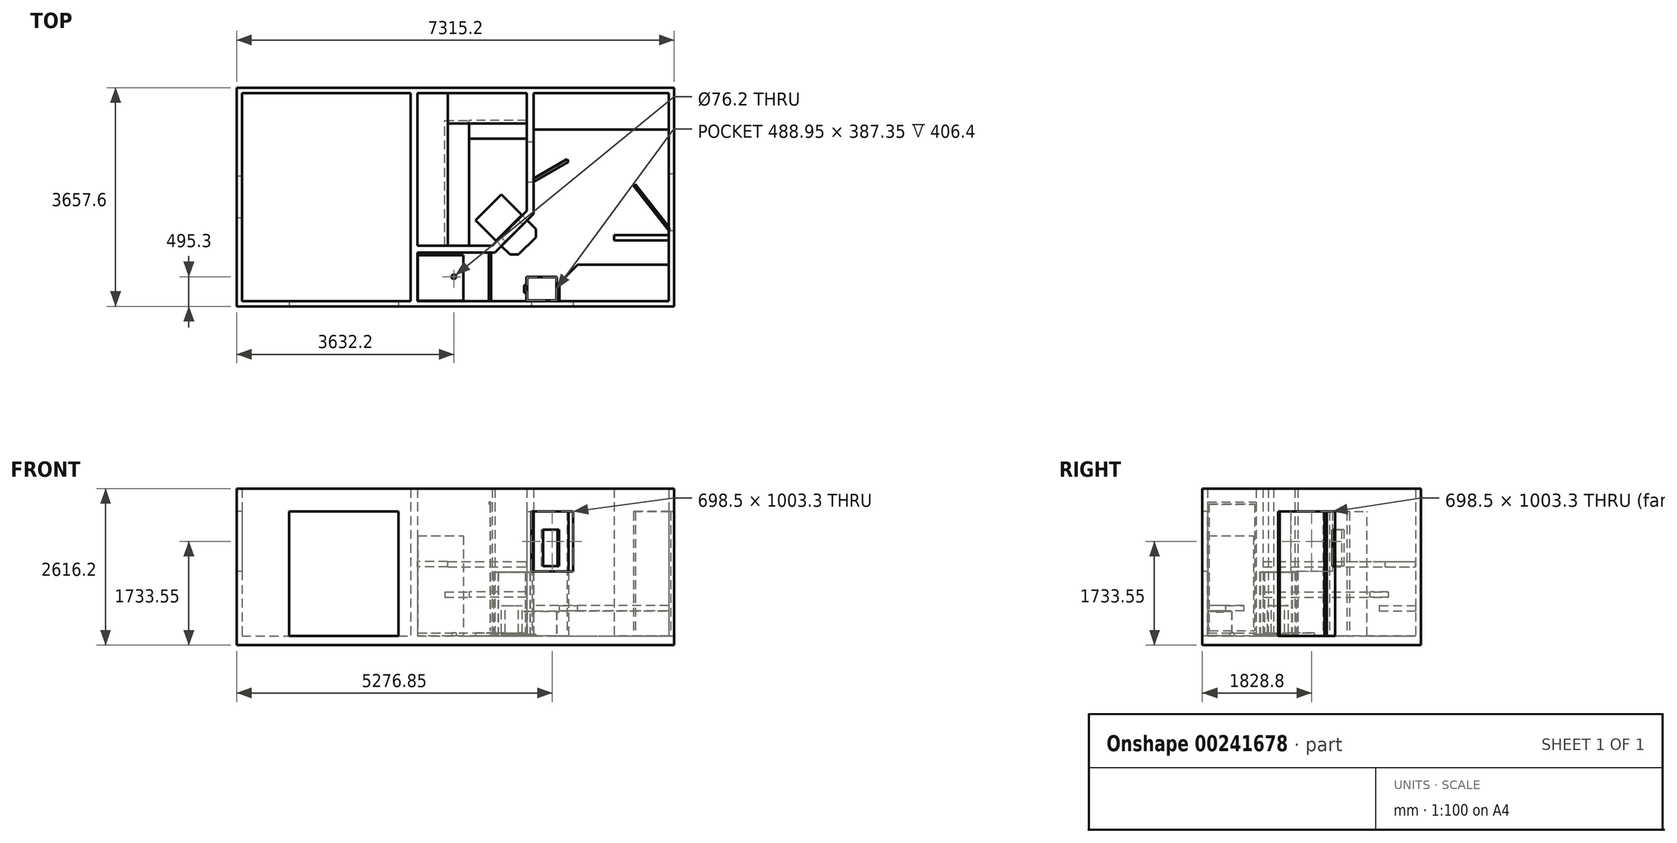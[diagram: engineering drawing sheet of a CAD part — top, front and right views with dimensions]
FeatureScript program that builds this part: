
annotation { "Feature Type Name" : "Feature", "Feature Type Description" : "" }
export const myFeature = defineFeature(function(context is Context, id is Id, definition is map)
    precondition{}
    {
        {
            var Q0;
            Q0=qCreatedBy(makeId("Top.planeOp"),FACE);
            var sketch = newSketch(context, id + "F0", { "sketchPlane" : qUnion([Q0])});
            skLineSegment(sketch, "E0.bottom", {"start": v(-3657.6, -1828.8) * mm, "end": v(3657.6, -1828.8) * mm});
            skLineSegment(sketch, "E0.top", {"start": v(-3657.6, 1828.8) * mm, "end": v(3657.6, 1828.8) * mm});
            skLineSegment(sketch, "E0.left", {"start": v(-3657.6, -1828.8) * mm, "end": v(-3657.6, 1828.8) * mm});
            skLineSegment(sketch, "E0.right", {"start": v(3657.6, -1828.8) * mm, "end": v(3657.6, 1828.8) * mm});
            skPoint(sketch, "E0.middle", {"position": v(0, 0) * mm});
            skSolve(sketch);
        }
        {
            var Q0;
            Q0=makeQuery(id+"F0.imprint","IMPRINT",FACE,{"disambiguationData":[TD([[makeQuery(id+"F0.imprint","IMPRINT",EDGE,{"derivedFrom":sQuery(id+"F0.wireOp",EDGE,"E0.bottom")}),1.0]])]});
            extrude(context, id + "F1", {"entities" : qUnion([Q0]), "depth" : 152.4 * mm});
        }
        {
            var Q0;
            Q0=makeQuery(id+"F1.opExtrude","CAP_FACE",FACE,{"disambiguationData":[OSD([sQuery(id+"F0.wireOp",EDGE,"E0.bottom"),sQuery(id+"F0.wireOp",EDGE,"E0.top"),sQuery(id+"F0.wireOp",EDGE,"E0.left"),sQuery(id+"F0.wireOp",EDGE,"E0.right")])],"isStart":false});
            var sketch = newSketch(context, id + "F2", { "sketchPlane" : qUnion([Q0])});
            skLineSegment(sketch, "E1.0", {"start": v(-3657.6, -1828.8) * mm, "end": v(-3657.6, 1828.8) * mm});
            skLineSegment(sketch, "E1.1", {"start": v(-3657.6, 1828.8) * mm, "end": v(3657.6, 1828.8) * mm});
            skLineSegment(sketch, "E1.2", {"start": v(3657.6, -1828.8) * mm, "end": v(3657.6, 1828.8) * mm});
            skLineSegment(sketch, "E1.3", {"start": v(-3657.6, -1828.8) * mm, "end": v(3657.6, -1828.8) * mm});
            skLineSegment(sketch, "E2.bottom", {"start": v(-3568.7, 1739.9) * mm, "end": v(3568.7, 1739.9) * mm});
            skLineSegment(sketch, "E2.top", {"start": v(-3568.7, -1739.9) * mm, "end": v(3568.7, -1739.9) * mm});
            skLineSegment(sketch, "E2.left", {"start": v(-3568.7, 1739.9) * mm, "end": v(-3568.7, -1739.9) * mm});
            skLineSegment(sketch, "E2.right", {"start": v(3568.7, 1739.9) * mm, "end": v(3568.7, -1739.9) * mm});
            skLineSegment(sketch, "E3", {"start": v(3568.7, 0) * mm, "end": v(0, 0) * mm, "construction": true});
            skSolve(sketch);
        }
        {
            var Q0;
            Q0 = qSketchRegion(id + "F2", true);
            extrude(context, id + "F3", {"entities" : qUnion([Q0]), "depth" : 2463.8 * mm});
        }
        {
            var Q0;
            Q0=makeQuery(id+"F3.opExtrude","SWEPT_FACE",FACE,{"disambiguationData":[OSD([sQuery(id+"F2.wireOp",EDGE,"E1.2")])]});
            var sketch = newSketch(context, id + "F4", { "sketchPlane" : qUnion([Q0])});
            skLineSegment(sketch, "E4.bottom", {"start": v(-558.8, 152.4) * mm, "end": v(393.7, 152.4) * mm});
            skLineSegment(sketch, "E4.top", {"start": v(-558.8, 2235.2) * mm, "end": v(393.7, 2235.2) * mm});
            skLineSegment(sketch, "E4.left", {"start": v(-558.8, 152.4) * mm, "end": v(-558.8, 2235.2) * mm});
            skLineSegment(sketch, "E4.right", {"start": v(393.7, 152.4) * mm, "end": v(393.7, 2235.2) * mm});
            skSolve(sketch);
        }
        {
            var Q0;
            Q0 = qSketchRegion(id + "F4", true);
            extrude(context, id + "F5", {"entities" : qUnion([Q0]), "operationType" : NewBodyOperationType.REMOVE, "endBound" : BoundingType.UP_TO_NEXT, "oppositeDirection" : true, "depth" : 25.4 * mm});
        }
        {
            var Q0;
            Q0=makeQuery(id+"F3.opExtrude","SWEPT_FACE",FACE,{"disambiguationData":[OSD([sQuery(id+"F2.wireOp",EDGE,"E1.3")])]});
            var sketch = newSketch(context, id + "F6", { "sketchPlane" : qUnion([Q0])});
            skLineSegment(sketch, "E5.bottom", {"start": v(-2781.3, 152.4) * mm, "end": v(-952.5, 152.4) * mm});
            skLineSegment(sketch, "E5.top", {"start": v(-2781.3, 2235.2) * mm, "end": v(-952.5, 2235.2) * mm});
            skLineSegment(sketch, "E5.left", {"start": v(-2781.3, 152.4) * mm, "end": v(-2781.3, 2235.2) * mm});
            skLineSegment(sketch, "E5.right", {"start": v(-952.5, 152.4) * mm, "end": v(-952.5, 2235.2) * mm});
            skLineSegment(sketch, "E6.bottom", {"start": v(1270, 2235.2) * mm, "end": v(1968.5, 2235.2) * mm});
            skLineSegment(sketch, "E6.top", {"start": v(1270, 1231.9) * mm, "end": v(1968.5, 1231.9) * mm});
            skLineSegment(sketch, "E6.left", {"start": v(1270, 2235.2) * mm, "end": v(1270, 1231.9) * mm});
            skLineSegment(sketch, "E6.right", {"start": v(1968.5, 2235.2) * mm, "end": v(1968.5, 1231.9) * mm});
            skSolve(sketch);
        }
        {
            var Q0;
            Q0 = qSketchRegion(id + "F6", true);
            extrude(context, id + "F7", {"entities" : qUnion([Q0]), "operationType" : NewBodyOperationType.REMOVE, "endBound" : BoundingType.UP_TO_NEXT, "oppositeDirection" : true, "depth" : 25.4 * mm});
        }
        {
            var Q0;
            Q0=makeQuery(id+"F3.opExtrude","SWEPT_FACE",FACE,{"disambiguationData":[OSD([sQuery(id+"F2.wireOp",EDGE,"E1.0")])]});
            var sketch = newSketch(context, id + "F8", { "sketchPlane" : qUnion([Q0])});
            skLineSegment(sketch, "E7.bottom", {"start": v(-349.25, 2235.2) * mm, "end": v(349.25, 2235.2) * mm});
            skLineSegment(sketch, "E7.top", {"start": v(-349.25, 1231.9) * mm, "end": v(349.25, 1231.9) * mm});
            skLineSegment(sketch, "E7.left", {"start": v(-349.25, 2235.2) * mm, "end": v(-349.25, 1231.9) * mm});
            skLineSegment(sketch, "E7.right", {"start": v(349.25, 2235.2) * mm, "end": v(349.25, 1231.9) * mm});
            skLineSegment(sketch, "E8", {"start": v(0, 2235.2) * mm, "end": v(0, 1231.9) * mm, "construction": true});
            skSolve(sketch);
        }
        {
            var Q0;
            Q0 = qSketchRegion(id + "F8", true);
            extrude(context, id + "F9", {"entities" : qUnion([Q0]), "operationType" : NewBodyOperationType.REMOVE, "endBound" : BoundingType.UP_TO_NEXT, "oppositeDirection" : true, "depth" : 25.4 * mm});
        }
        {
            var Q0;
            Q0=makeQuery(id+"F1.opExtrude","CAP_FACE",FACE,{"disambiguationData":[OSD([sQuery(id+"F0.wireOp",EDGE,"E0.bottom"),sQuery(id+"F0.wireOp",EDGE,"E0.top"),sQuery(id+"F0.wireOp",EDGE,"E0.left"),sQuery(id+"F0.wireOp",EDGE,"E0.right")])],"isStart":false});
            var sketch = newSketch(context, id + "F10", { "sketchPlane" : qUnion([Q0])});
            skLineSegment(sketch, "E9.bottom", {"start": v(-749.3, -1739.9) * mm, "end": v(-635, -1739.9) * mm});
            skLineSegment(sketch, "E9.top", {"start": v(-749.3, 1739.9) * mm, "end": v(-635, 1739.9) * mm});
            skLineSegment(sketch, "E9.left", {"start": v(-749.3, -1739.9) * mm, "end": v(-749.3, 1739.9) * mm});
            skLineSegment(sketch, "E9.right", {"start": v(-635, -1739.9) * mm, "end": v(-635, 1739.9) * mm});
            skLineSegment(sketch, "E10.top", {"start": v(1193.8, 1739.9) * mm, "end": v(1308.1, 1739.9) * mm});
            skLineSegment(sketch, "E11", {"start": v(1193.8, 1739.9) * mm, "end": v(1193.8, -233.18) * mm});
            skLineSegment(sketch, "E12", {"start": v(1193.8, -233.18) * mm, "end": v(614.18, -812.8) * mm});
            skLineSegment(sketch, "E13", {"start": v(614.18, -812.8) * mm, "end": v(-635, -812.8) * mm});
            skLineSegment(sketch, "E14", {"start": v(-635, -812.8) * mm, "end": v(-635, -927.1) * mm});
            skLineSegment(sketch, "E15", {"start": v(-635, -927.1) * mm, "end": v(661.52, -927.1) * mm});
            skLineSegment(sketch, "E16", {"start": v(661.52, -927.1) * mm, "end": v(1308.1, -280.52) * mm});
            skLineSegment(sketch, "E17", {"start": v(1308.1, -280.52) * mm, "end": v(1308.1, 1739.9) * mm});
            skSolve(sketch);
        }
        {
            var Q0;
            Q0 = qSketchRegion(id + "F10", true);
            var Q1;
            Q1=makeQuery(id+"F3.opExtrude","CAP_FACE",FACE,{"disambiguationData":[OSD([sQuery(id+"F2.wireOp",EDGE,"E1.0"),sQuery(id+"F2.wireOp",EDGE,"E1.1"),sQuery(id+"F2.wireOp",EDGE,"E1.2"),sQuery(id+"F2.wireOp",EDGE,"E1.3"),sQuery(id+"F2.wireOp",EDGE,"E2.bottom"),sQuery(id+"F2.wireOp",EDGE,"E2.top"),sQuery(id+"F2.wireOp",EDGE,"E2.left"),sQuery(id+"F2.wireOp",EDGE,"E2.right")])],"isStart":false});
            extrude(context, id + "F11", {"entities" : qUnion([Q0]), "endBound" : BoundingType.UP_TO_SURFACE, "endBoundEntityFace" : qUnion([Q1]), "depth" : 25.4 * mm});
        }
        {
            var Q0;
            Q0=makeQuery(id+"F1.opExtrude","CAP_FACE",FACE,{"disambiguationData":[OSD([sQuery(id+"F0.wireOp",EDGE,"E0.bottom"),sQuery(id+"F0.wireOp",EDGE,"E0.top"),sQuery(id+"F0.wireOp",EDGE,"E0.left"),sQuery(id+"F0.wireOp",EDGE,"E0.right")])],"isStart":false});
            var sketch = newSketch(context, id + "F12", { "sketchPlane" : qUnion([Q0])});
            skLineSegment(sketch, "E18.bottom", {"start": v(3568.7, -723.9) * mm, "end": v(2654.3, -723.9) * mm});
            skLineSegment(sketch, "E18.top", {"start": v(3568.7, -635) * mm, "end": v(2654.3, -635) * mm});
            skLineSegment(sketch, "E18.left", {"start": v(3568.7, -723.9) * mm, "end": v(3568.7, -635) * mm});
            skLineSegment(sketch, "E18.right", {"start": v(2654.3, -723.9) * mm, "end": v(2654.3, -635) * mm});
            skSolve(sketch);
        }
        {
            var Q0;
            Q0 = qSketchRegion(id + "F12", true);
            var Q1;
            Q1=makeQuery(id+"F3.opExtrude","CAP_FACE",FACE,{"disambiguationData":[OSD([sQuery(id+"F2.wireOp",EDGE,"E1.0"),sQuery(id+"F2.wireOp",EDGE,"E1.1"),sQuery(id+"F2.wireOp",EDGE,"E1.2"),sQuery(id+"F2.wireOp",EDGE,"E1.3"),sQuery(id+"F2.wireOp",EDGE,"E2.bottom"),sQuery(id+"F2.wireOp",EDGE,"E2.top"),sQuery(id+"F2.wireOp",EDGE,"E2.left"),sQuery(id+"F2.wireOp",EDGE,"E2.right")])],"isStart":false});
            extrude(context, id + "F13", {"entities" : qUnion([Q0]), "endBound" : BoundingType.UP_TO_SURFACE, "endBoundEntityFace" : qUnion([Q1]), "depth" : 25.4 * mm});
        }
        {
            var Q0;
            Q0=makeQuery(id+"F11.opExtrude","SWEPT_FACE",FACE,{"disambiguationData":[OSD([sQuery(id+"F10.wireOp",EDGE,"E17")])]});
            var sketch = newSketch(context, id + "F14", { "sketchPlane" : qUnion([Q0])});
            skLineSegment(sketch, "E19.bottom", {"start": v(254, 152.4) * mm, "end": v(927.1, 152.4) * mm});
            skLineSegment(sketch, "E19.top", {"start": v(254, 2235.2) * mm, "end": v(927.1, 2235.2) * mm});
            skLineSegment(sketch, "E19.left", {"start": v(254, 152.4) * mm, "end": v(254, 2235.2) * mm});
            skLineSegment(sketch, "E19.right", {"start": v(927.1, 152.4) * mm, "end": v(927.1, 2235.2) * mm});
            skSolve(sketch);
        }
        {
            var Q0;
            Q0 = qSketchRegion(id + "F14", true);
            extrude(context, id + "F15", {"entities" : qUnion([Q0]), "operationType" : NewBodyOperationType.REMOVE, "endBound" : BoundingType.UP_TO_NEXT, "oppositeDirection" : true, "depth" : 25.4 * mm});
        }
        {
            var Q0;
            Q0=qCreatedBy(makeId("Front.planeOp"),FACE);
            var sketch = newSketch(context, id + "F16", { "sketchPlane" : qUnion([Q0])});
            skLineSegment(sketch, "E20.bottom", {"start": v(-635, 152.4) * mm, "end": v(-596.9, 152.4) * mm});
            skLineSegment(sketch, "E20.top", {"start": v(-635, 1397) * mm, "end": v(-596.9, 1397) * mm});
            skLineSegment(sketch, "E20.left", {"start": v(-635, 152.4) * mm, "end": v(-635, 1397) * mm});
            skLineSegment(sketch, "E20.right", {"start": v(-596.9, 152.4) * mm, "end": v(-596.9, 1397) * mm});
            skSolve(sketch);
        }
        {
            var Q0;
            Q0 = qSketchRegion(id + "F16", true);
            extrude(context, id + "F17", {"entities" : qUnion([Q0]), "endBound" : BoundingType.SYMMETRIC, "depth" : 88.9 * mm});
        }
        {
            var Q0;
            Q0=makeQuery(id+"F17.opExtrude","SWEPT_BODY",BODY,{"disambiguationData":[OSD([sQuery(id+"F16.wireOp",EDGE,"E20.bottom"),sQuery(id+"F16.wireOp",EDGE,"E20.top"),sQuery(id+"F16.wireOp",EDGE,"E20.left"),sQuery(id+"F16.wireOp",EDGE,"E20.right")])]});
            deleteBodies(context, id + "F18", {"entities" : qUnion([Q0])});
        }
        {
            var Q0;
            Q0=qCreatedBy(makeId("Front.planeOp"),FACE);
            var sketch = newSketch(context, id + "F19", { "sketchPlane" : qUnion([Q0])});
            skLineSegment(sketch, "E21.bottom", {"start": v(-635, 1397) * mm, "end": v(-127, 1397) * mm});
            skLineSegment(sketch, "E21.top", {"start": v(-635, 1308.1) * mm, "end": v(-127, 1308.1) * mm});
            skLineSegment(sketch, "E21.left", {"start": v(-635, 1397) * mm, "end": v(-635, 1308.1) * mm});
            skLineSegment(sketch, "E21.right", {"start": v(-127, 1397) * mm, "end": v(-127, 1308.1) * mm});
            skSolve(sketch);
        }
        {
            var Q0;
            Q0 = qSketchRegion(id + "F19", true);
            extrude(context, id + "F20", {"entities" : qUnion([Q0]), "depth" : 812.8 * mm, "hasSecondDirection" : true, "secondDirectionBound" : SecondDirectionBoundingType.UP_TO_NEXT, "secondDirectionOppositeDirection" : true, "secondDirectionDepth" : 25.4 * mm});
        }
        {
            var Q0;
            Q0=makeQuery(id+"F20.opExtrude","SWEPT_FACE",FACE,{"disambiguationData":[OSD([sQuery(id+"F19.wireOp",EDGE,"E21.bottom")])]});
            var sketch = newSketch(context, id + "F21", { "sketchPlane" : qUnion([Q0])});
            skLineSegment(sketch, "E22.top", {"start": v(-127, 1231.9) * mm, "end": v(1193.8, 1231.9) * mm});
            skLineSegment(sketch, "E22.left", {"start": v(-127, 1231.9) * mm, "end": v(-127, 1739.9) * mm});
            skLineSegment(sketch, "E22.right", {"start": v(1193.8, 1231.9) * mm, "end": v(1193.8, 1739.9) * mm});
            skLineSegment(sketch, "E23", {"start": v(1193.8, 1739.9) * mm, "end": v(-127, 1739.9) * mm});
            skSolve(sketch);
        }
        {
            var Q0;
            Q0 = qSketchRegion(id + "F21", true);
            var Q1;
            Q1=makeQuery(id+"F20.opExtrude","CAP_VERTEX",VERTEX,{"disambiguationData":[OSD([sQuery(id+"F2.wireOp",EDGE,"E2.top"),sQuery(id+"F19.wireOp",EDGE,"E21.top"),sQuery(id+"F19.wireOp",EDGE,"E21.right")])],"isStart":false});
            extrude(context, id + "F22", {"entities" : qUnion([Q0]), "endBound" : BoundingType.UP_TO_VERTEX, "oppositeDirection" : true, "endBoundEntityVertex" : qUnion([Q1]), "depth" : 25.4 * mm});
        }
        {
            var Q0;
            Q0=qCreatedBy(makeId("Front.planeOp"),FACE);
            var sketch = newSketch(context, id + "F23", { "sketchPlane" : qUnion([Q0])});
            skLineSegment(sketch, "E24.bottom", {"start": v(-177.8, 889) * mm, "end": v(228.6, 889) * mm});
            skLineSegment(sketch, "E24.top", {"start": v(-177.8, 800.1) * mm, "end": v(228.6, 800.1) * mm});
            skLineSegment(sketch, "E24.left", {"start": v(-177.8, 889) * mm, "end": v(-177.8, 800.1) * mm});
            skLineSegment(sketch, "E24.right", {"start": v(228.6, 889) * mm, "end": v(228.6, 800.1) * mm});
            skSolve(sketch);
        }
        {
            var Q0;
            Q0 = qSketchRegion(id + "F23", true);
            extrude(context, id + "F24", {"entities" : qUnion([Q0]), "depth" : 812.8 * mm, "hasSecondDirection" : true, "secondDirectionOppositeDirection" : true, "secondDirectionDepth" : 1282.7 * mm});
        }
        {
            var Q0;
            Q0=makeQuery(id+"F24.opExtrude","SWEPT_FACE",FACE,{"disambiguationData":[OSD([sQuery(id+"F23.wireOp",EDGE,"E24.bottom")])]});
            var sketch = newSketch(context, id + "F25", { "sketchPlane" : qUnion([Q0])});
            skLineSegment(sketch, "E25.bottom", {"start": v(1193.8, 1282.7) * mm, "end": v(228.6, 1282.7) * mm});
            skLineSegment(sketch, "E25.top", {"start": v(228.6, 977.9) * mm, "end": v(1193.8, 977.9) * mm});
            skLineSegment(sketch, "E25.left", {"start": v(228.6, 1282.7) * mm, "end": v(228.6, 977.9) * mm});
            skLineSegment(sketch, "E25.right", {"start": v(1193.8, 1282.7) * mm, "end": v(1193.8, 977.9) * mm});
            skSolve(sketch);
        }
        {
            var Q0;
            Q0=makeQuery(id+"F3.opExtrude","SWEPT_FACE",FACE,{"disambiguationData":[OSD([sQuery(id+"F2.wireOp",EDGE,"E2.bottom")])]});
            var sketch = newSketch(context, id + "F26", { "sketchPlane" : qUnion([Q0])});
            skLineSegment(sketch, "E26.bottom", {"start": v(3568.7, 660.4) * mm, "end": v(1308.1, 660.4) * mm});
            skLineSegment(sketch, "E26.top", {"start": v(1308.1, 571.5) * mm, "end": v(3568.7, 571.5) * mm});
            skLineSegment(sketch, "E26.left", {"start": v(3568.7, 660.4) * mm, "end": v(3568.7, 571.5) * mm});
            skLineSegment(sketch, "E26.right", {"start": v(1308.1, 660.4) * mm, "end": v(1308.1, 571.5) * mm});
            skSolve(sketch);
        }
        {
            var Q0;
            Q0 = qSketchRegion(id + "F26", true);
            extrude(context, id + "F27", {"entities" : qUnion([Q0]), "depth" : 609.6 * mm});
        }
        {
            var Q0;
            Q0=makeQuery(id+"F27.opExtrude","SWEPT_FACE",FACE,{"disambiguationData":[OSD([sQuery(id+"F26.wireOp",EDGE,"E26.bottom")])]});
            var sketch = newSketch(context, id + "F28", { "sketchPlane" : qUnion([Q0])});
            skLineSegment(sketch, "E27.bottom", {"start": v(1308.1, 1130.3) * mm, "end": v(1714.5, 1130.3) * mm});
            skLineSegment(sketch, "E27.top", {"start": v(1308.1, 114.3) * mm, "end": v(1714.5, 114.3) * mm});
            skLineSegment(sketch, "E27.left", {"start": v(1308.1, 114.3) * mm, "end": v(1308.1, 1130.3) * mm});
            skLineSegment(sketch, "E27.right", {"start": v(1714.5, 114.3) * mm, "end": v(1714.5, 1130.3) * mm});
            skSolve(sketch);
        }
        {
            var Q0;
            Q0 = qSketchRegion(id + "F25", true);
            var Q1;
            Q1=makeQuery(id+"F24.opExtrude","CAP_VERTEX",VERTEX,{"disambiguationData":[OSD([sQuery(id+"F23.wireOp",EDGE,"E24.top"),sQuery(id+"F23.wireOp",EDGE,"E24.right")])],"isStart":true});
            extrude(context, id + "F29", {"entities" : qUnion([Q0]), "endBound" : BoundingType.UP_TO_VERTEX, "oppositeDirection" : true, "endBoundEntityVertex" : qUnion([Q1]), "depth" : 25.4 * mm});
        }
        {
            var Q0;
            Q0=makeQuery(id+"F1.opExtrude","CAP_FACE",FACE,{"disambiguationData":[OSD([sQuery(id+"F0.wireOp",EDGE,"E0.bottom"),sQuery(id+"F0.wireOp",EDGE,"E0.top"),sQuery(id+"F0.wireOp",EDGE,"E0.left"),sQuery(id+"F0.wireOp",EDGE,"E0.right")])],"isStart":false});
            var sketch = newSketch(context, id + "F30", { "sketchPlane" : qUnion([Q0])});
            skLineSegment(sketch, "E28", {"start": v(1282.7, 298) * mm, "end": v(1308.1, 254) * mm});
            skLineSegment(sketch, "E29", {"start": v(1308.1, 254) * mm, "end": v(1891.02, 590.55) * mm});
            skLineSegment(sketch, "E30", {"start": v(1891.02, 590.55) * mm, "end": v(1865.62, 634.54) * mm});
            skLineSegment(sketch, "E31", {"start": v(1865.62, 634.54) * mm, "end": v(1282.7, 298) * mm});
            skSolve(sketch);
        }
        {
            var Q0;
            Q0 = qSketchRegion(id + "F30", true);
            extrude(context, id + "F31", {"entities" : qUnion([Q0]), "depth" : 2082.8 * mm});
        }
        {
            var Q0;
            Q0=makeQuery(id+"F1.opExtrude","CAP_FACE",FACE,{"disambiguationData":[OSD([sQuery(id+"F0.wireOp",EDGE,"E0.bottom"),sQuery(id+"F0.wireOp",EDGE,"E0.top"),sQuery(id+"F0.wireOp",EDGE,"E0.left"),sQuery(id+"F0.wireOp",EDGE,"E0.right")])],"isStart":false});
            var sketch = newSketch(context, id + "F32", { "sketchPlane" : qUnion([Q0])});
            skLineSegment(sketch, "E32", {"start": v(3568.7, -558.8) * mm, "end": v(3598.59, -535.17) * mm});
            skLineSegment(sketch, "E33", {"start": v(3598.59, -535.17) * mm, "end": v(3007.81, 211.99) * mm});
            skLineSegment(sketch, "E34", {"start": v(3007.81, 211.99) * mm, "end": v(2977.93, 188.36) * mm});
            skLineSegment(sketch, "E35", {"start": v(2977.93, 188.36) * mm, "end": v(3568.7, -558.8) * mm});
            skSolve(sketch);
        }
        {
            var Q0;
            Q0 = qSketchRegion(id + "F32", true);
            extrude(context, id + "F33", {"entities" : qUnion([Q0]), "depth" : 2082.8 * mm});
        }
        {
            var Q0;
            Q0=makeQuery(id+"F1.opExtrude","CAP_FACE",FACE,{"disambiguationData":[OSD([sQuery(id+"F0.wireOp",EDGE,"E0.bottom"),sQuery(id+"F0.wireOp",EDGE,"E0.top"),sQuery(id+"F0.wireOp",EDGE,"E0.left"),sQuery(id+"F0.wireOp",EDGE,"E0.right")])],"isStart":false});
            var sketch = newSketch(context, id + "F34", { "sketchPlane" : qUnion([Q0])});
            skLineSegment(sketch, "E36", {"start": v(-635, -1739.9) * mm, "end": v(-635, -971.55) * mm});
            skLineSegment(sketch, "E37", {"start": v(-635, -1739.9) * mm, "end": v(133.35, -1739.9) * mm});
            skLineSegment(sketch, "E38.0", {"start": v(-628.65, -1733.55) * mm, "end": v(133.35, -1733.55) * mm});
            skLineSegment(sketch, "E38.1", {"start": v(-628.65, -1733.55) * mm, "end": v(-628.65, -971.55) * mm});
            skLineSegment(sketch, "E39", {"start": v(-635, -971.55) * mm, "end": v(-628.65, -971.55) * mm});
            skLineSegment(sketch, "E40", {"start": v(133.35, -1739.9) * mm, "end": v(133.35, -1733.55) * mm});
            skSolve(sketch);
        }
        {
            var Q0;
            Q0 = qSketchRegion(id + "F34", true);
            extrude(context, id + "F35", {"entities" : qUnion([Q0]), "depth" : 1676.4 * mm});
        }
        {
            var Q0;
            Q0=makeQuery(id+"F1.opExtrude","CAP_FACE",FACE,{"disambiguationData":[OSD([sQuery(id+"F0.wireOp",EDGE,"E0.bottom"),sQuery(id+"F0.wireOp",EDGE,"E0.top"),sQuery(id+"F0.wireOp",EDGE,"E0.left"),sQuery(id+"F0.wireOp",EDGE,"E0.right")])],"isStart":false});
            var sketch = newSketch(context, id + "F36", { "sketchPlane" : qUnion([Q0])});
            skLineSegment(sketch, "E41.bottom", {"start": v(-635, -1739.9) * mm, "end": v(133.35, -1739.9) * mm});
            skLineSegment(sketch, "E41.top", {"start": v(-635, -971.55) * mm, "end": v(133.35, -971.55) * mm});
            skLineSegment(sketch, "E41.left", {"start": v(-635, -1739.9) * mm, "end": v(-635, -971.55) * mm});
            skLineSegment(sketch, "E41.right", {"start": v(133.35, -1739.9) * mm, "end": v(133.35, -971.55) * mm});
            skSolve(sketch);
        }
        {
            var Q0;
            Q0 = qSketchRegion(id + "F36", true);
            extrude(context, id + "F37", {"entities" : qUnion([Q0]), "operationType" : NewBodyOperationType.ADD, "depth" : 50.8 * mm});
        }
        {
            var Q0;
            Q0=makeQuery(id+"F11.opExtrude","SWEPT_FACE",FACE,{"disambiguationData":[OSD([sQuery(id+"F10.wireOp",EDGE,"E16")])]});
            var sketch = newSketch(context, id + "F38", { "sketchPlane" : qUnion([Q0])});
            skLineSegment(sketch, "E42.bottom", {"start": v(66.2, 152.4) * mm, "end": v(472.6, 152.4) * mm});
            skLineSegment(sketch, "E42.top", {"start": v(66.2, 660.4) * mm, "end": v(472.6, 660.4) * mm});
            skLineSegment(sketch, "E42.left", {"start": v(66.2, 152.4) * mm, "end": v(66.2, 660.4) * mm});
            skLineSegment(sketch, "E42.right", {"start": v(472.6, 152.4) * mm, "end": v(472.6, 660.4) * mm});
            skLineSegment(sketch, "E43", {"start": v(269.4, 660.4) * mm, "end": v(269.4, 152.4) * mm, "construction": true});
            skSolve(sketch);
        }
        {
            var Q0;
            Q0 = qSketchRegion(id + "F38", true);
            extrude(context, id + "F39", {"entities" : qUnion([Q0]), "operationType" : NewBodyOperationType.REMOVE, "endBound" : BoundingType.UP_TO_NEXT, "oppositeDirection" : true, "depth" : 50.8 * mm});
        }
        {
            var Q0;
            Q0=makeQuery(id+"F1.opExtrude","CAP_FACE",FACE,{"disambiguationData":[OSD([sQuery(id+"F0.wireOp",EDGE,"E0.bottom"),sQuery(id+"F0.wireOp",EDGE,"E0.top"),sQuery(id+"F0.wireOp",EDGE,"E0.left"),sQuery(id+"F0.wireOp",EDGE,"E0.right")])],"isStart":false});
            var sketch = newSketch(context, id + "F40", { "sketchPlane" : qUnion([Q0])});
            skLineSegment(sketch, "E44.bottom", {"start": v(-635, -1739.9) * mm, "end": v(584.2, -1739.9) * mm});
            skLineSegment(sketch, "E44.top", {"start": v(-635, -927.1) * mm, "end": v(584.2, -927.1) * mm});
            skLineSegment(sketch, "E44.left", {"start": v(-635, -1739.9) * mm, "end": v(-635, -927.1) * mm});
            skLineSegment(sketch, "E44.right", {"start": v(584.2, -1739.9) * mm, "end": v(584.2, -927.1) * mm});
            skCircle(sketch, "E45", {"center": v(-25.4, -1333.5) * mm, "radius": 38.1 * mm});
            skLineSegment(sketch, "E46", {"start": v(-25.4, -927.1) * mm, "end": v(-25.4, -1739.9) * mm, "construction": true});
            skSolve(sketch);
        }
        {
            var Q0;
            Q0 = qSketchRegion(id + "F40", true);
            extrude(context, id + "F41", {"entities" : qUnion([Q0]), "depth" : 50.8 * mm});
        }
        {
            var Q0;
            Q0=makeQuery(id+"F3.opExtrude","SWEPT_FACE",FACE,{"disambiguationData":[OSD([sQuery(id+"F2.wireOp",EDGE,"E2.top")])]});
            var sketch = newSketch(context, id + "F42", { "sketchPlane" : qUnion([Q0])});
            skLineSegment(sketch, "E47.bottom", {"start": v(-3568.7, 660.4) * mm, "end": v(-1739.9, 660.4) * mm});
            skLineSegment(sketch, "E47.top", {"start": v(-3568.7, 571.5) * mm, "end": v(-1739.9, 571.5) * mm});
            skLineSegment(sketch, "E47.left", {"start": v(-3568.7, 660.4) * mm, "end": v(-3568.7, 571.5) * mm});
            skLineSegment(sketch, "E47.right", {"start": v(-1739.9, 660.4) * mm, "end": v(-1739.9, 571.5) * mm});
            skSolve(sketch);
        }
        {
            var Q0;
            Q0 = qSketchRegion(id + "F42", true);
            extrude(context, id + "F43", {"entities" : qUnion([Q0]), "depth" : 609.6 * mm});
        }
        {
            var Q0;
            Q0=makeQuery(id+"F43.opExtrude","SWEPT_FACE",FACE,{"disambiguationData":[OSD([sQuery(id+"F42.wireOp",EDGE,"E47.bottom")])]});
            var sketch = newSketch(context, id + "F44", { "sketchPlane" : qUnion([Q0])});
            skLineSegment(sketch, "E48", {"start": v(1739.9, -1130.3) * mm, "end": v(1739.9, -1435.1) * mm});
            skLineSegment(sketch, "E49", {"start": v(1739.9, -1435.1) * mm, "end": v(2044.7, -1130.3) * mm});
            skLineSegment(sketch, "E50", {"start": v(2044.7, -1130.3) * mm, "end": v(1739.9, -1130.3) * mm});
            skSolve(sketch);
        }
        {
            var Q0;
            Q0 = qSketchRegion(id + "F44", true);
            extrude(context, id + "F45", {"entities" : qUnion([Q0]), "operationType" : NewBodyOperationType.REMOVE, "endBound" : BoundingType.UP_TO_NEXT, "oppositeDirection" : true, "depth" : 25.4 * mm});
        }
        {
            var Q0;
            Q0=makeQuery(id+"F31.opExtrude","SWEPT_FACE",FACE,{"disambiguationData":[OSD([sQuery(id+"F30.wireOp",EDGE,"E29")])]});
            var sketch = newSketch(context, id + "F46", { "sketchPlane" : qUnion([Q0])});
            skLineSegment(sketch, "E51.bottom", {"start": v(1444, 1930.4) * mm, "end": v(1748.8, 1930.4) * mm});
            skLineSegment(sketch, "E51.top", {"start": v(1444, 1320.8) * mm, "end": v(1748.8, 1320.8) * mm});
            skLineSegment(sketch, "E51.left", {"start": v(1444, 1930.4) * mm, "end": v(1444, 1320.8) * mm});
            skLineSegment(sketch, "E51.right", {"start": v(1748.8, 1930.4) * mm, "end": v(1748.8, 1320.8) * mm});
            skLineSegment(sketch, "E52", {"start": v(1596.4, 2235.2) * mm, "end": v(1596.4, 1930.4) * mm, "construction": true});
            skSolve(sketch);
        }
        {
            var Q0;
            Q0 = qSketchRegion(id + "F46", true);
            extrude(context, id + "F47", {"entities" : qUnion([Q0]), "operationType" : NewBodyOperationType.REMOVE, "endBound" : BoundingType.UP_TO_NEXT, "oppositeDirection" : true, "depth" : 25.4 * mm});
        }
        {
            var Q0;
            Q0=makeQuery(id+"F1.opExtrude","CAP_FACE",FACE,{"disambiguationData":[OSD([sQuery(id+"F0.wireOp",EDGE,"E0.bottom"),sQuery(id+"F0.wireOp",EDGE,"E0.top"),sQuery(id+"F0.wireOp",EDGE,"E0.left"),sQuery(id+"F0.wireOp",EDGE,"E0.right")])],"isStart":false});
            var sketch = newSketch(context, id + "F48", { "sketchPlane" : qUnion([Q0])});
            skLineSegment(sketch, "E53", {"start": v(769.28, -819.34) * mm, "end": v(338.23, -388.28) * mm});
            skLineSegment(sketch, "E54", {"start": v(338.23, -388.28) * mm, "end": v(769.28, 42.77) * mm});
            skLineSegment(sketch, "E55", {"start": v(769.28, 42.77) * mm, "end": v(1200.34, -388.28) * mm});
            skLineSegment(sketch, "E56", {"start": v(1200.34, -388.28) * mm, "end": v(769.28, -819.34) * mm});
            skLineSegment(sketch, "E57", {"start": v(903.99, -522.99) * mm, "end": v(984.81, -603.81) * mm, "construction": true});
            skSolve(sketch);
        }
        {
            var Q0;
            Q0 = qSketchRegion(id + "F48", true);
            extrude(context, id + "F49", {"entities" : qUnion([Q0]), "depth" : 50.8 * mm});
        }
        {
            var Q0;
            Q0=makeQuery(id+"F11.opExtrude","SWEPT_FACE",FACE,{"disambiguationData":[OSD([sQuery(id+"F10.wireOp",EDGE,"E16")])]});
            var sketch = newSketch(context, id + "F50", { "sketchPlane" : qUnion([Q0])});
            skLineSegment(sketch, "E58.bottom", {"start": v(-35.4, 203.2) * mm, "end": v(574.2, 203.2) * mm});
            skLineSegment(sketch, "E58.top", {"start": v(-35.4, 152.4) * mm, "end": v(574.2, 152.4) * mm});
            skLineSegment(sketch, "E58.left", {"start": v(-35.4, 203.2) * mm, "end": v(-35.4, 152.4) * mm});
            skLineSegment(sketch, "E58.right", {"start": v(574.2, 203.2) * mm, "end": v(574.2, 152.4) * mm});
            skSolve(sketch);
        }
        {
            var Q0;
            Q0 = qSketchRegion(id + "F50", true);
            extrude(context, id + "F51", {"entities" : qUnion([Q0]), "operationType" : NewBodyOperationType.REMOVE, "oppositeDirection" : true, "depth" : 127 * mm});
        }
        {
            var Q0;
            Q0=makeQuery(id+"F1.opExtrude","CAP_FACE",FACE,{"disambiguationData":[OSD([sQuery(id+"F0.wireOp",EDGE,"E0.bottom"),sQuery(id+"F0.wireOp",EDGE,"E0.top"),sQuery(id+"F0.wireOp",EDGE,"E0.left"),sQuery(id+"F0.wireOp",EDGE,"E0.right")])],"isStart":false});
            var sketch = newSketch(context, id + "F52", { "sketchPlane" : qUnion([Q0])});
            skLineSegment(sketch, "E59", {"start": v(637.1, -789.88) * mm, "end": v(644.95, -797.74) * mm});
            skLineSegment(sketch, "E60", {"start": v(644.95, -797.74) * mm, "end": v(1178.74, -263.95) * mm});
            skLineSegment(sketch, "E61", {"start": v(1178.74, -263.95) * mm, "end": v(1170.88, -256.1) * mm});
            skLineSegment(sketch, "E62", {"start": v(1170.88, -256.1) * mm, "end": v(637.1, -789.88) * mm});
            skLineSegment(sketch, "E63", {"start": v(553.76, -172.76) * mm, "end": v(903.99, -522.99) * mm, "construction": true});
            skLineSegment(sketch, "E64", {"start": v(717.92, -870.7) * mm, "end": v(710.06, -862.85) * mm});
            skLineSegment(sketch, "E65", {"start": v(710.06, -862.85) * mm, "end": v(1243.85, -329.06) * mm});
            skLineSegment(sketch, "E66", {"start": v(1243.85, -329.06) * mm, "end": v(1251.7, -336.92) * mm});
            skLineSegment(sketch, "E67", {"start": v(1251.7, -336.92) * mm, "end": v(717.92, -870.7) * mm});
            skSolve(sketch);
        }
        {
            var Q0;
            Q0 = qSketchRegion(id + "F52", true);
            extrude(context, id + "F53", {"entities" : qUnion([Q0]), "operationType" : NewBodyOperationType.REMOVE, "depth" : 1066.8 * mm});
        }
        {
            var Q0;
            Q0=makeQuery(id+"F1.opExtrude","CAP_FACE",FACE,{"disambiguationData":[OSD([sQuery(id+"F0.wireOp",EDGE,"E0.bottom"),sQuery(id+"F0.wireOp",EDGE,"E0.top"),sQuery(id+"F0.wireOp",EDGE,"E0.left"),sQuery(id+"F0.wireOp",EDGE,"E0.right")])],"isStart":false});
            var sketch = newSketch(context, id + "F54", { "sketchPlane" : qUnion([Q0])});
            skLineSegment(sketch, "E68", {"start": v(769.28, -819.34) * mm, "end": v(912.97, -963.02) * mm});
            skLineSegment(sketch, "E69", {"start": v(912.97, -963.02) * mm, "end": v(1056.65, -963.02) * mm});
            skLineSegment(sketch, "E70", {"start": v(1056.65, -963.02) * mm, "end": v(1344.02, -675.65) * mm});
            skLineSegment(sketch, "E71", {"start": v(1344.02, -675.65) * mm, "end": v(1344.02, -531.97) * mm});
            skLineSegment(sketch, "E72", {"start": v(1344.02, -531.97) * mm, "end": v(1200.34, -388.28) * mm});
            skLineSegment(sketch, "E73", {"start": v(1200.34, -388.28) * mm, "end": v(769.28, -819.34) * mm});
            skLineSegment(sketch, "E74", {"start": v(984.81, -603.81) * mm, "end": v(1200.34, -819.34) * mm, "construction": true});
            skSolve(sketch);
        }
        {
            var Q0;
            Q0 = qSketchRegion(id + "F54", true);
            extrude(context, id + "F55", {"entities" : qUnion([Q0]), "depth" : 25.4 * mm});
        }
        {
            var Q0;
            Q0=makeQuery(id+"F11.opExtrude","SWEPT_FACE",FACE,{"disambiguationData":[OSD([sQuery(id+"F10.wireOp",EDGE,"E15")])]});
            var sketch = newSketch(context, id + "F56", { "sketchPlane" : qUnion([Q0])});
            skCircle(sketch, "E75", {"center": v(576.53, 2375.54) * mm, "radius": 19.05 * mm});
            skSolve(sketch);
        }
        {
            var Q0;
            Q0 = qSketchRegion(id + "F56", true);
            extrude(context, id + "F57", {"entities" : qUnion([Q0]), "endBound" : BoundingType.UP_TO_NEXT, "depth" : 25.4 * mm});
        }
        {
            var Q0;
            Q0=makeQuery(id+"F41.opExtrude","SWEPT_FACE",FACE,{"disambiguationData":[OSD([sQuery(id+"F40.wireOp",EDGE,"E44.right")])]});
            var sketch = newSketch(context, id + "F58", { "sketchPlane" : qUnion([Q0])});
            skLineSegment(sketch, "E76.bottom", {"start": v(-1714.5, 2363.56) * mm, "end": v(-952.5, 2363.56) * mm});
            skLineSegment(sketch, "E76.top", {"start": v(-1714.5, 238.7) * mm, "end": v(-952.5, 238.7) * mm});
            skLineSegment(sketch, "E76.left", {"start": v(-1714.5, 2363.56) * mm, "end": v(-1714.5, 238.7) * mm});
            skLineSegment(sketch, "E76.right", {"start": v(-952.5, 2363.56) * mm, "end": v(-952.5, 238.7) * mm});
            skSolve(sketch);
        }
        {
            var Q0;
            Q0 = qSketchRegion(id + "F58", true);
            extrude(context, id + "F59", {"entities" : qUnion([Q0]), "oppositeDirection" : true, "depth" : 3.17 * mm});
        }
        {
            var Q0;
            Q0=makeQuery(id+"F1.opExtrude","CAP_FACE",FACE,{"disambiguationData":[OSD([sQuery(id+"F0.wireOp",EDGE,"E0.bottom"),sQuery(id+"F0.wireOp",EDGE,"E0.top"),sQuery(id+"F0.wireOp",EDGE,"E0.left"),sQuery(id+"F0.wireOp",EDGE,"E0.right")])],"isStart":false});
            var sketch = newSketch(context, id + "F60", { "sketchPlane" : qUnion([Q0])});
            skLineSegment(sketch, "E77.bottom", {"start": v(1696.48, -1739.9) * mm, "end": v(1188.48, -1739.9) * mm});
            skLineSegment(sketch, "E77.top", {"start": v(1696.48, -1333.5) * mm, "end": v(1188.48, -1333.5) * mm});
            skLineSegment(sketch, "E77.left", {"start": v(1696.48, -1739.9) * mm, "end": v(1696.48, -1333.5) * mm});
            skLineSegment(sketch, "E77.right", {"start": v(1188.48, -1739.9) * mm, "end": v(1188.48, -1333.5) * mm});
            skSolve(sketch);
        }
        {
            var Q0;
            Q0 = qSketchRegion(id + "F60", true);
            extrude(context, id + "F61", {"entities" : qUnion([Q0]), "depth" : 9.52 * mm});
        }
        {
            var Q0;
            Q0=makeQuery(id+"F61.opExtrude","CAP_FACE",FACE,{"disambiguationData":[OSD([sQuery(id+"F60.wireOp",EDGE,"E77.bottom"),sQuery(id+"F60.wireOp",EDGE,"E77.top"),sQuery(id+"F60.wireOp",EDGE,"E77.left"),sQuery(id+"F60.wireOp",EDGE,"E77.right")])],"isStart":false});
            var sketch = newSketch(context, id + "F62", { "sketchPlane" : qUnion([Q0])});
            skLineSegment(sketch, "E78", {"start": v(1696.48, -1739.9) * mm, "end": v(1696.48, -1333.5) * mm});
            skLineSegment(sketch, "E79", {"start": v(1696.48, -1333.5) * mm, "end": v(1188.48, -1333.5) * mm});
            skLineSegment(sketch, "E80", {"start": v(1188.48, -1333.5) * mm, "end": v(1188.48, -1739.9) * mm});
            skLineSegment(sketch, "E81", {"start": v(1188.48, -1739.9) * mm, "end": v(1696.48, -1739.9) * mm});
            skLineSegment(sketch, "E82.0", {"start": v(1198, -1730.38) * mm, "end": v(1686.96, -1730.38) * mm});
            skLineSegment(sketch, "E82.1", {"start": v(1198, -1343.03) * mm, "end": v(1198, -1730.38) * mm});
            skLineSegment(sketch, "E82.2", {"start": v(1686.96, -1343.03) * mm, "end": v(1198, -1343.03) * mm});
            skLineSegment(sketch, "E82.3", {"start": v(1686.96, -1730.38) * mm, "end": v(1686.96, -1343.03) * mm});
            skSolve(sketch);
        }
        {
            var Q0;
            Q0 = qSketchRegion(id + "F62", true);
            extrude(context, id + "F63", {"entities" : qUnion([Q0]), "operationType" : NewBodyOperationType.ADD, "depth" : 406.4 * mm});
        }
        {
            var Q0;
            Q0=makeQuery(id+"F63.opExtrude","CAP_FACE",FACE,{"disambiguationData":[OSD([sQuery(id+"F62.wireOp",EDGE,"E78"),sQuery(id+"F62.wireOp",EDGE,"E79"),sQuery(id+"F62.wireOp",EDGE,"E80"),sQuery(id+"F62.wireOp",EDGE,"E81"),sQuery(id+"F62.wireOp",EDGE,"E82.0"),sQuery(id+"F62.wireOp",EDGE,"E82.1"),sQuery(id+"F62.wireOp",EDGE,"E82.2"),sQuery(id+"F62.wireOp",EDGE,"E82.3")])],"isStart":false});
            var sketch = newSketch(context, id + "F64", { "sketchPlane" : qUnion([Q0])});
            skLineSegment(sketch, "E83.bottom", {"start": v(1188.48, -1600.2) * mm, "end": v(1163.08, -1600.2) * mm});
            skLineSegment(sketch, "E83.top", {"start": v(1188.48, -1473.2) * mm, "end": v(1163.08, -1473.2) * mm});
            skLineSegment(sketch, "E83.left", {"start": v(1188.48, -1600.2) * mm, "end": v(1188.48, -1473.2) * mm});
            skLineSegment(sketch, "E83.right", {"start": v(1150.38, -1587.5) * mm, "end": v(1150.38, -1485.9) * mm});
            skLineSegment(sketch, "E84.bottom", {"start": v(1696.48, -1600.2) * mm, "end": v(1721.88, -1600.2) * mm});
            skLineSegment(sketch, "E84.top", {"start": v(1696.48, -1473.2) * mm, "end": v(1721.88, -1473.2) * mm});
            skLineSegment(sketch, "E84.left", {"start": v(1696.48, -1600.2) * mm, "end": v(1696.48, -1473.2) * mm});
            skLineSegment(sketch, "E84.right", {"start": v(1734.58, -1587.5) * mm, "end": v(1734.58, -1485.9) * mm});
            skPoint(sketch, "E85.visualSharp", {"position": v(1734.58, -1600.2) * mm});
            skArc(sketch, "E85.filletArc", {"start": v(1721.88, -1600.2) * mm, "mid": v(1730.86, -1596.48) * mm, "end": v(1734.58, -1587.5) * mm});
            skPoint(sketch, "E86.visualSharp", {"position": v(1734.58, -1473.2) * mm});
            skArc(sketch, "E86.filletArc", {"start": v(1734.58, -1485.9) * mm, "mid": v(1730.86, -1476.92) * mm, "end": v(1721.88, -1473.2) * mm});
            skPoint(sketch, "E87.visualSharp", {"position": v(1150.38, -1600.2) * mm});
            skArc(sketch, "E87.filletArc", {"start": v(1150.38, -1587.5) * mm, "mid": v(1154.1, -1596.48) * mm, "end": v(1163.08, -1600.2) * mm});
            skPoint(sketch, "E88.visualSharp", {"position": v(1150.38, -1473.2) * mm});
            skArc(sketch, "E88.filletArc", {"start": v(1163.08, -1473.2) * mm, "mid": v(1154.1, -1476.92) * mm, "end": v(1150.38, -1485.9) * mm});
            skPoint(sketch, "E89", {"position": v(1686.96, -1536.7) * mm});
            skLineSegment(sketch, "E90", {"start": v(1696.48, -1536.7) * mm, "end": v(1188.48, -1536.7) * mm, "construction": true});
            skSolve(sketch);
        }
        {
            var Q0;
            Q0 = qSketchRegion(id + "F64", true);
            extrude(context, id + "F65", {"entities" : qUnion([Q0]), "operationType" : NewBodyOperationType.ADD, "oppositeDirection" : true, "depth" : 12.7 * mm});
        }
    });
